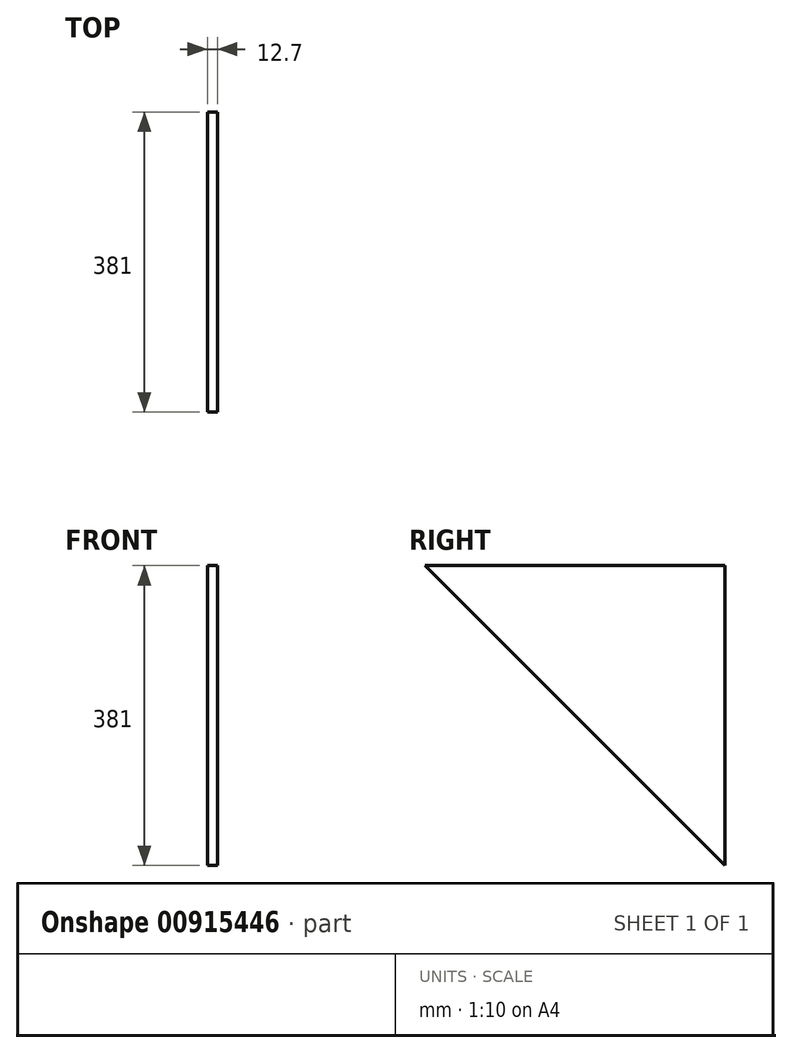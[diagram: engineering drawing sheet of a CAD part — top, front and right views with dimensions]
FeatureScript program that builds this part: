
annotation { "Feature Type Name" : "Feature", "Feature Type Description" : "" }
export const myFeature = defineFeature(function(context is Context, id is Id, definition is map)
    precondition{}
    {
        {
            var Q0;
            Q0=qCreatedBy(makeId("Right.planeOp"),FACE);
            var sketch = newSketch(context, id + "F0", { "sketchPlane" : qUnion([Q0])});
            skLineSegment(sketch, "E0.bottom", {"start": v(190.5, 190.5) * mm, "end": v(-190.5, 190.5) * mm});
            skLineSegment(sketch, "E0.left", {"start": v(190.5, 190.5) * mm, "end": v(190.5, -190.5) * mm});
            skPoint(sketch, "E0.middle", {"position": v(0, 0) * mm});
            skLineSegment(sketch, "E1", {"start": v(-190.5, 190.5) * mm, "end": v(190.5, -190.5) * mm});
            skSolve(sketch);
        }
        {
            var Q0;
            Q0=makeQuery(id+"F0.imprint","IMPRINT",FACE,{"disambiguationData":[TD([[makeQuery(id+"F0.imprint","IMPRINT",EDGE,{"derivedFrom":sQuery(id+"F0.wireOp",EDGE,"E0.bottom")}),1.0]])]});
            extrude(context, id + "F1", {"entities" : qUnion([Q0]), "depth" : 12.7 * mm, "offsetDistance" : 25.4 * mm});
        }
    });
